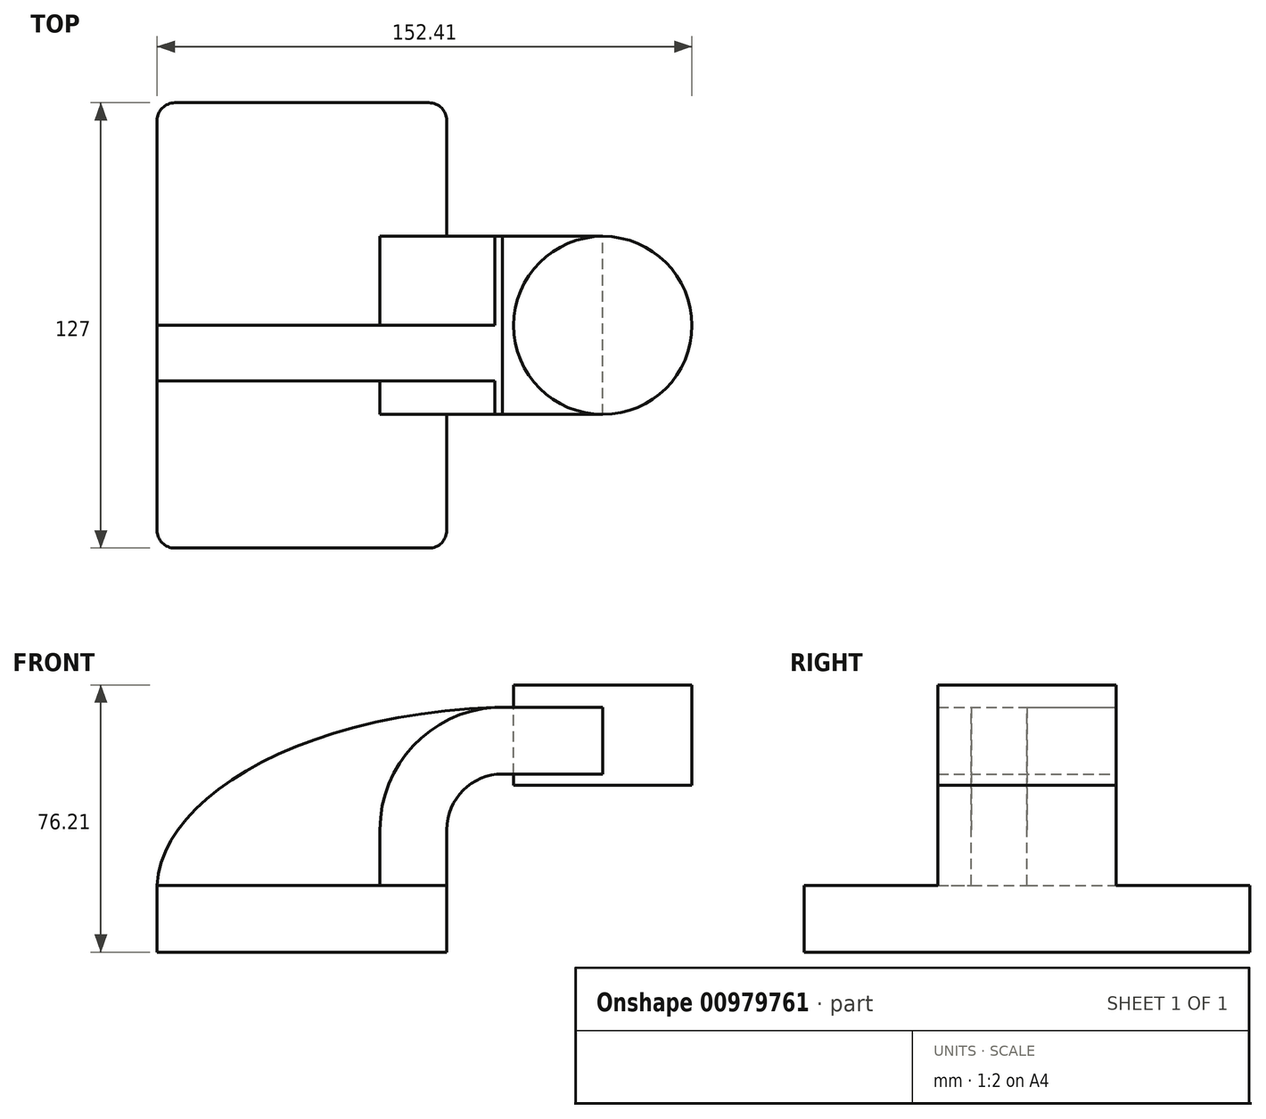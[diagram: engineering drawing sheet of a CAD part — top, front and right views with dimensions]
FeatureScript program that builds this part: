
annotation { "Feature Type Name" : "Feature", "Feature Type Description" : "" }
export const myFeature = defineFeature(function(context is Context, id is Id, definition is map)
    precondition{}
    {
        {
            var Q0;
            Q0=qCreatedBy(makeId("Front.planeOp"),FACE);
            var sketch = newSketch(context, id + "F0", { "sketchPlane" : qUnion([Q0])});
            skLineSegment(sketch, "E0.bottom", {"start": v(41.27, 9.53) * mm, "end": v(-41.28, 9.53) * mm});
            skLineSegment(sketch, "E0.top", {"start": v(41.28, -9.52) * mm, "end": v(-41.27, -9.52) * mm});
            skLineSegment(sketch, "E0.left", {"start": v(41.28, 9.53) * mm, "end": v(41.28, -9.52) * mm});
            skLineSegment(sketch, "E0.right", {"start": v(-41.28, 9.53) * mm, "end": v(-41.27, -9.52) * mm});
            skPoint(sketch, "E0.middle", {"position": v(0, 0) * mm});
            skLineSegment(sketch, "E1.bottom", {"start": v(60.32, 66.68) * mm, "end": v(111.12, 66.68) * mm});
            skLineSegment(sketch, "E1.top", {"start": v(60.32, 38.1) * mm, "end": v(111.12, 38.1) * mm});
            skLineSegment(sketch, "E1.left", {"start": v(60.32, 66.68) * mm, "end": v(60.32, 38.1) * mm});
            skLineSegment(sketch, "E1.right", {"start": v(111.12, 66.68) * mm, "end": v(111.12, 38.1) * mm});
            skPoint(sketch, "E1.middle", {"position": v(85.72, 52.39) * mm});
            skLineSegment(sketch, "E2", {"start": v(41.27, 9.53) * mm, "end": v(41.27, 25.4) * mm});
            skArc(sketch, "E3", {"start": v(41.27, 25.4) * mm, "mid": v(45.92, 36.63) * mm, "end": v(57.15, 41.28) * mm});
            skLineSegment(sketch, "E4", {"start": v(57.15, 41.28) * mm, "end": v(85.72, 41.28) * mm});
            skLineSegment(sketch, "E5.0", {"start": v(57.15, 60.33) * mm, "end": v(85.72, 60.33) * mm});
            skArc(sketch, "E5.1", {"start": v(22.22, 25.4) * mm, "mid": v(32.45, 50.1) * mm, "end": v(57.15, 60.33) * mm});
            skLineSegment(sketch, "E5.2", {"start": v(22.22, 9.53) * mm, "end": v(22.22, 25.4) * mm});
            skLineSegment(sketch, "E6", {"start": v(85.72, 60.33) * mm, "end": v(85.72, 41.28) * mm});
            skFitSpline(sketch, "E7", {"points": [v(-41.28, 9.53) * mm, v(57.15, 60.33) * mm], "startDerivative": vector(3.68, 75.06) * mm, "endDerivative": vector(171.45, 4.46) * mm});
            skLineSegment(sketch, "E8", {"start": v(85.72, 41.28) * mm, "end": v(85.72, 66.68) * mm});
            skLineSegment(sketch, "E9", {"start": v(85.72, 41.28) * mm, "end": v(85.72, 38.1) * mm});
            skSolve(sketch);
        }
        {
            var Q0;
            Q0=makeQuery(id+"F0.imprint","IMPRINT",FACE,{"disambiguationData":[TD([[makeQuery(id+"F0.imprint","IMPRINT",EDGE,{"derivedFrom":sQuery(id+"F0.wireOp",EDGE,"E0.top")}),-1.0]])]});
            extrude(context, id + "F1", {"entities" : qUnion([Q0]), "endBound" : BoundingType.SYMMETRIC, "depth" : 127 * mm, "offsetDistance" : 25.4 * mm});
        }
        {
            var Q0;
            {var subQ1=sQuery(id+"F0.wireOp",EDGE,"E2");Q0=makeQuery(id+"F0.imprint","IMPRINT",FACE,{"disambiguationData":[TD([[makeQuery(id+"F0.imprint","IMPRINT",EDGE,{"derivedFrom":subQ1}),1.0]])]});}
            var Q1;
            {var subQ0=sQuery(id+"F0.wireOp",EDGE,"E5.0");var subQ1=sQuery(id+"F0.wireOp",EDGE,"E1.left");var subQ2=makeQuery(id+"F0.imprint","INTERSECT",VERTEX,{"derivedFrom":[subQ1,subQ0]});Q1=makeQuery(id+"F0.imprint","IMPRINT",FACE,{"disambiguationData":[TD([[makeQuery(id+"F0.imprint","IMPRINT",EDGE,{"disambiguationData":[TD([[subQ2,-1.0]])],"derivedFrom":subQ1}),1.0]])]});}
            extrude(context, id + "F2", {"entities" : qUnion([Q0, Q1]), "operationType" : NewBodyOperationType.ADD, "endBound" : BoundingType.SYMMETRIC, "depth" : 50.8 * mm, "offsetDistance" : 25.4 * mm});
        }
        {
            var Q0;
            {var subQ3=sQuery(id+"F0.wireOp",EDGE,"E5.2");Q0=makeQuery(id+"F0.imprint","IMPRINT",FACE,{"disambiguationData":[TD([[makeQuery(id+"F0.imprint","IMPRINT",EDGE,{"derivedFrom":subQ3}),1.0]])]});}
            extrude(context, id + "F3", {"entities" : qUnion([Q0]), "operationType" : NewBodyOperationType.ADD, "depth" : 15.88 * mm, "offsetDistance" : 25.4 * mm});
        }
        {
            var Q0;
            {var subQ3=sQuery(id+"F0.wireOp",EDGE,"E1.right");Q0=makeQuery(id+"F0.imprint","IMPRINT",FACE,{"disambiguationData":[TD([[makeQuery(id+"F0.imprint","IMPRINT",EDGE,{"derivedFrom":subQ3}),-1.0]])]});}
            var Q1;
            Q1=sQuery(id+"F0.wireOp",EDGE,"E6");
            revolve(context, id + "F4", {"surfaceOperationType" : NewSurfaceOperationType.NEW, "entities" : qUnion([Q0]), "axis" : qUnion([Q1]), "revolveType" : RevolveType.FULL});
        }
        {
            var Q0;
            Q0=makeQuery(id+"F1.opExtrude","CAP_EDGE",EDGE,{"disambiguationData":[OSD([sQuery(id+"F0.wireOp",EDGE,"E0.left")])],"isStart":false});
            var Q1;
            Q1=makeQuery(id+"F1.opExtrude","CAP_EDGE",EDGE,{"disambiguationData":[OSD([sQuery(id+"F0.wireOp",EDGE,"E0.right")])],"isStart":false});
            var Q2;
            Q2=makeQuery(id+"F1.opExtrude","CAP_EDGE",EDGE,{"disambiguationData":[OSD([sQuery(id+"F0.wireOp",EDGE,"E0.left")])],"isStart":true});
            var Q3;
            Q3=makeQuery(id+"F1.opExtrude","CAP_EDGE",EDGE,{"disambiguationData":[OSD([sQuery(id+"F0.wireOp",EDGE,"E0.right")])],"isStart":true});
            fillet(context, id + "F5", {"entities" : qUnion([Q0, Q1, Q2, Q3]), "radius" : 5.08 * mm, "tangentPropagation" : true, "allowEdgeOverflow" : false});
        }
    });
